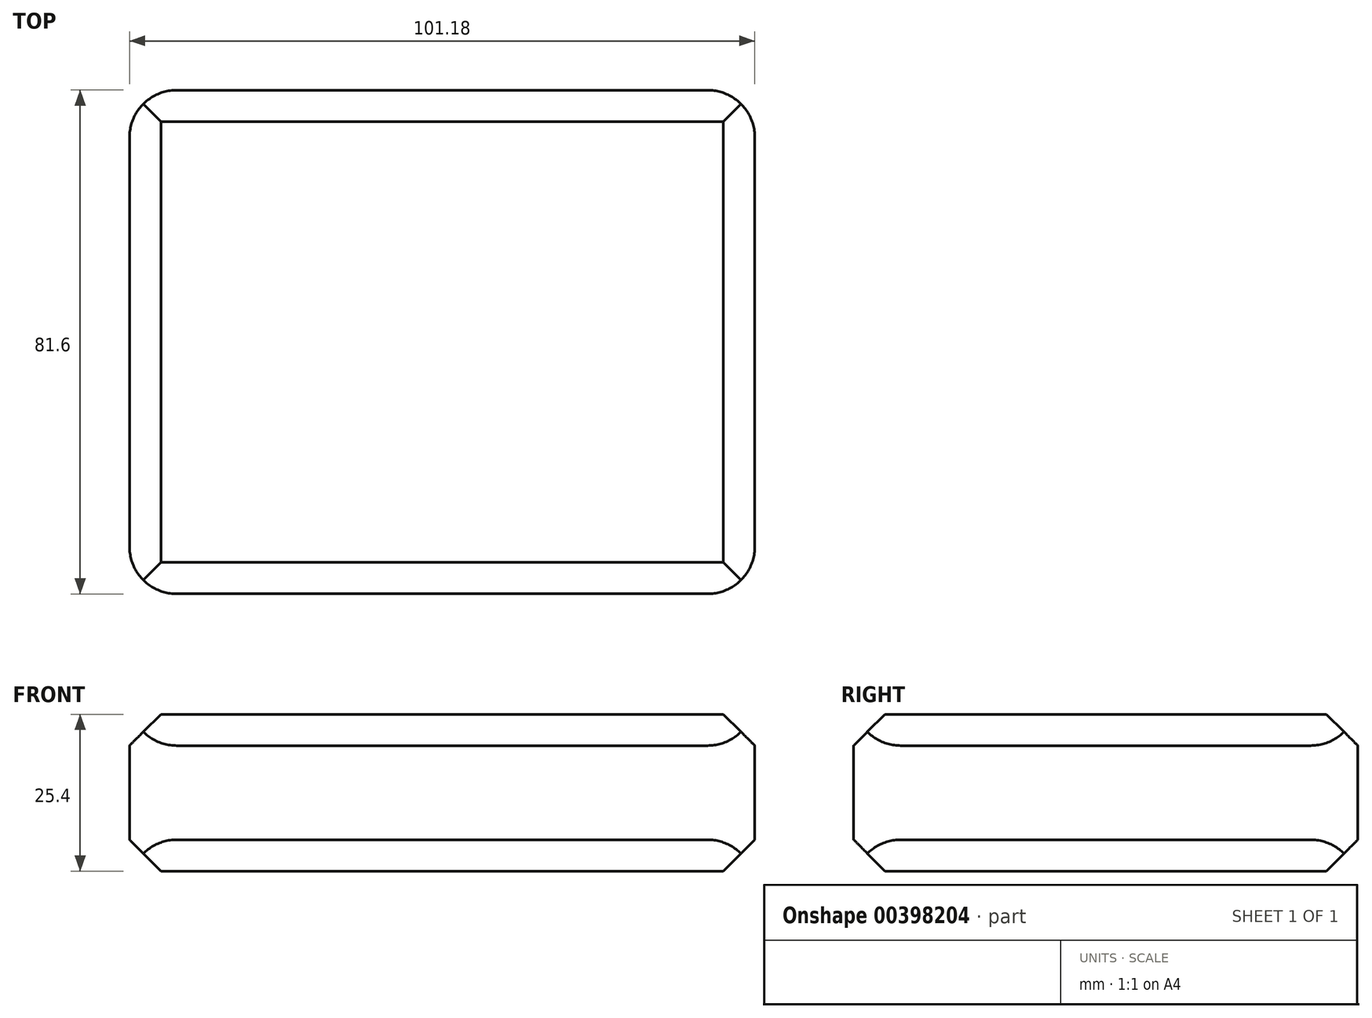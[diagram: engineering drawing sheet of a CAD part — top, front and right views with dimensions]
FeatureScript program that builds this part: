
annotation { "Feature Type Name" : "Feature", "Feature Type Description" : "" }
export const myFeature = defineFeature(function(context is Context, id is Id, definition is map)
    precondition{}
    {
        {
            var Q0;
            Q0=qCreatedBy(makeId("Top.planeOp"),FACE);
            var sketch = newSketch(context, id + "F0", { "sketchPlane" : qUnion([Q0])});
            skLineSegment(sketch, "E0.bottom", {"start": v(50.6, -40.8) * mm, "end": v(-50.6, -40.8) * mm});
            skLineSegment(sketch, "E0.top", {"start": v(50.6, 40.8) * mm, "end": v(-50.6, 40.8) * mm});
            skLineSegment(sketch, "E0.left", {"start": v(50.6, -40.8) * mm, "end": v(50.6, 40.8) * mm});
            skLineSegment(sketch, "E0.right", {"start": v(-50.6, -40.8) * mm, "end": v(-50.6, 40.8) * mm});
            skPoint(sketch, "E0.middle", {"position": v(0, 0) * mm});
            skSolve(sketch);
        }
        {
            var Q0;
            Q0=makeQuery(id+"F0.imprint","IMPRINT",FACE,{"disambiguationData":[TD([[makeQuery(id+"F0.imprint","IMPRINT",EDGE,{"derivedFrom":sQuery(id+"F0.wireOp",EDGE,"E0.bottom")}),-1.0]])]});
            extrude(context, id + "F1", {"entities" : qUnion([Q0]), "depth" : 25.4 * mm});
        }
        {
            var Q0;
            Q0=makeQuery(id+"F1.opExtrude","CAP_EDGE",EDGE,{"disambiguationData":[OSD([sQuery(id+"F0.wireOp",EDGE,"E0.bottom")])],"isStart":true});
            var Q1;
            Q1=makeQuery(id+"F1.opExtrude","CAP_EDGE",EDGE,{"disambiguationData":[OSD([sQuery(id+"F0.wireOp",EDGE,"E0.right")])],"isStart":true});
            var Q2;
            Q2=makeQuery(id+"F1.opExtrude","CAP_EDGE",EDGE,{"disambiguationData":[OSD([sQuery(id+"F0.wireOp",EDGE,"E0.top")])],"isStart":true});
            var Q3;
            Q3=makeQuery(id+"F1.opExtrude","CAP_EDGE",EDGE,{"disambiguationData":[OSD([sQuery(id+"F0.wireOp",EDGE,"E0.left")])],"isStart":true});
            chamfer(context, id + "F2", {"entities" : qUnion([Q0, Q1, Q2, Q3]), "width" : 5.08 * mm, "tangentPropagation" : true});
        }
        {
            var Q0;
            Q0=makeQuery(id+"F1.opExtrude","CAP_EDGE",EDGE,{"disambiguationData":[OSD([sQuery(id+"F0.wireOp",EDGE,"E0.bottom")])],"isStart":false});
            var Q1;
            Q1=makeQuery(id+"F1.opExtrude","CAP_EDGE",EDGE,{"disambiguationData":[OSD([sQuery(id+"F0.wireOp",EDGE,"E0.left")])],"isStart":false});
            var Q2;
            Q2=makeQuery(id+"F1.opExtrude","CAP_EDGE",EDGE,{"disambiguationData":[OSD([sQuery(id+"F0.wireOp",EDGE,"E0.top")])],"isStart":false});
            var Q3;
            Q3=makeQuery(id+"F1.opExtrude","CAP_EDGE",EDGE,{"disambiguationData":[OSD([sQuery(id+"F0.wireOp",EDGE,"E0.right")])],"isStart":false});
            chamfer(context, id + "F3", {"entities" : qUnion([Q0, Q1, Q2, Q3]), "width" : 5.08 * mm, "tangentPropagation" : true});
        }
        {
            var Q0;
            Q0=makeQuery(id+"F1.opExtrude","SWEPT_EDGE",EDGE,{"disambiguationData":[OSD([sQuery(id+"F0.wireOp",EDGE,"E0.bottom"),sQuery(id+"F0.wireOp",EDGE,"E0.right")])]});
            var Q1;
            Q1=makeQuery(id+"F1.opExtrude","SWEPT_EDGE",EDGE,{"disambiguationData":[OSD([sQuery(id+"F0.wireOp",EDGE,"E0.top"),sQuery(id+"F0.wireOp",EDGE,"E0.right")])]});
            var Q2;
            Q2=makeQuery(id+"F1.opExtrude","SWEPT_EDGE",EDGE,{"disambiguationData":[OSD([sQuery(id+"F0.wireOp",EDGE,"E0.top"),sQuery(id+"F0.wireOp",EDGE,"E0.left")])]});
            var Q3;
            Q3=makeQuery(id+"F1.opExtrude","SWEPT_EDGE",EDGE,{"disambiguationData":[OSD([sQuery(id+"F0.wireOp",EDGE,"E0.bottom"),sQuery(id+"F0.wireOp",EDGE,"E0.left")])]});
            fillet(context, id + "F4", {"entities" : qUnion([Q0, Q1, Q2, Q3]), "radius" : 7.62 * mm, "tangentPropagation" : true, "allowEdgeOverflow" : false});
        }
    });
